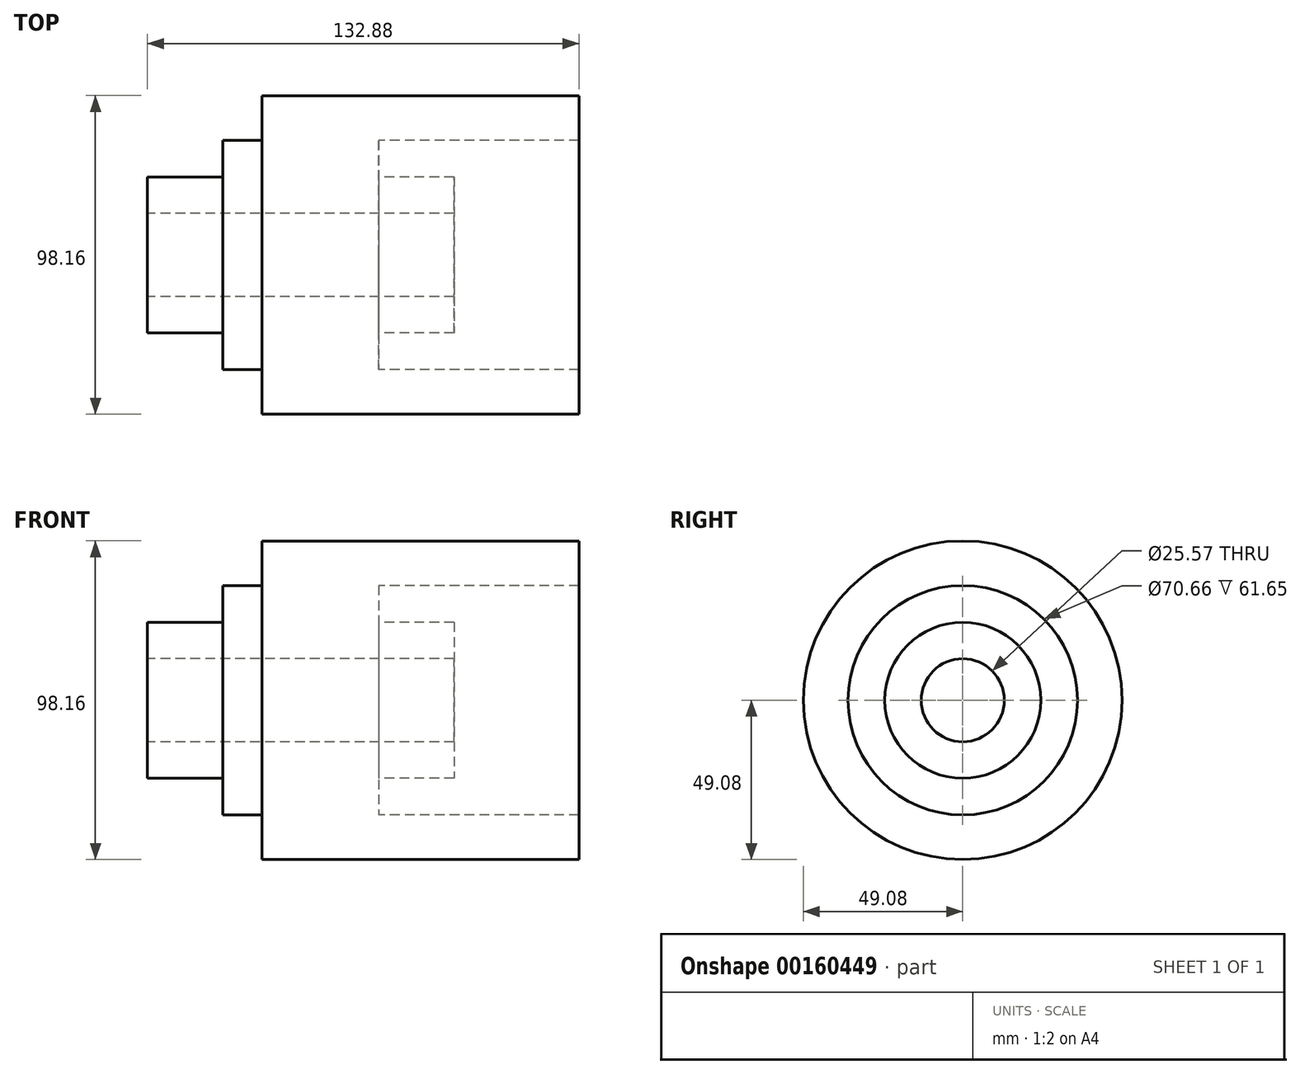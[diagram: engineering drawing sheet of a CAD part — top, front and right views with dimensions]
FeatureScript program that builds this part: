
annotation { "Feature Type Name" : "Feature", "Feature Type Description" : "" }
export const myFeature = defineFeature(function(context is Context, id is Id, definition is map)
    precondition{}
    {
        {
            var Q0;
            Q0=qCreatedBy(makeId("Front.planeOp"),FACE);
            var sketch = newSketch(context, id + "F0", { "sketchPlane" : qUnion([Q0])});
            skLineSegment(sketch, "E0", {"start": v(0, 0) * mm, "end": v(-47.2, 0) * mm});
            skLineSegment(sketch, "E1", {"start": v(-47.2, 0) * mm, "end": v(-47.2, 24.02) * mm});
            skLineSegment(sketch, "E2", {"start": v(-47.2, 24.02) * mm, "end": v(-24.02, 24.02) * mm});
            skLineSegment(sketch, "E3", {"start": v(-24.02, 24.02) * mm, "end": v(-24.02, 35.33) * mm});
            skLineSegment(sketch, "E4", {"start": v(-24.02, 35.33) * mm, "end": v(-12.01, 35.33) * mm});
            skLineSegment(sketch, "E5", {"start": v(12.01, 35.33) * mm, "end": v(24.02, 35.33) * mm});
            skLineSegment(sketch, "E6", {"start": v(24.02, 35.33) * mm, "end": v(24.02, 24.02) * mm});
            skLineSegment(sketch, "E7", {"start": v(24.02, 24.02) * mm, "end": v(47.2, 24.02) * mm});
            skLineSegment(sketch, "E8", {"start": v(47.2, 24.02) * mm, "end": v(47.2, 0) * mm});
            skLineSegment(sketch, "E9", {"start": v(0, 0) * mm, "end": v(47.2, 0) * mm});
            skLineSegment(sketch, "E10", {"start": v(-12.01, 35.33) * mm, "end": v(-12.01, 49.08) * mm});
            skLineSegment(sketch, "E11", {"start": v(-12.01, 49.08) * mm, "end": v(0, 49.08) * mm});
            skLineSegment(sketch, "E12", {"start": v(0, 49.08) * mm, "end": v(12.01, 49.08) * mm});
            skPoint(sketch, "E12.endSnap0", {"position": v(12.01, 35.33) * mm});
            skLineSegment(sketch, "E13", {"start": v(12.01, 49.08) * mm, "end": v(12.01, 35.33) * mm});
            skPoint(sketch, "E14.orphan", {"position": v(0, 35.33) * mm});
            skSolve(sketch);
        }
        {
            var Q0;
            Q0=makeQuery(id+"F0.imprint","IMPRINT",FACE,{"disambiguationData":[TD([[makeQuery(id+"F0.imprint","IMPRINT",EDGE,{"derivedFrom":sQuery(id+"F0.wireOp",EDGE,"E0")}),-1.0]])]});
            var Q1;
            Q1=sQuery(id+"F0.wireOp",EDGE,"E9");
            revolve(context, id + "F1", {"entities" : qUnion([Q0]), "axis" : qUnion([Q1]), "revolveType" : RevolveType.FULL});
        }
        {
            var Q0;
            Q0=makeQuery(id+"F1.opRevolve","SWEPT_FACE",FACE,{"disambiguationData":[OSD([sQuery(id+"F0.wireOp",EDGE,"E1")])]});
            var sketch = newSketch(context, id + "F2", { "sketchPlane" : qUnion([Q0])});
            skCircle(sketch, "E15", {"center": v(0, 0) * mm, "radius": 12.79 * mm});
            skSolve(sketch);
        }
        {
            var Q0;
            Q0=makeQuery(id+"F2.imprint","IMPRINT",FACE,{"disambiguationData":[TD([[makeQuery(id+"F2.imprint","IMPRINT",EDGE,{"derivedFrom":sQuery(id+"F2.wireOp",EDGE,"E15")}),1.0]])]});
            extrude(context, id + "F3", {"entities" : qUnion([Q0]), "operationType" : NewBodyOperationType.REMOVE, "endBound" : BoundingType.THROUGH_ALL, "oppositeDirection" : true, "depth" : 25.4 * mm});
        }
        {
            var Q0;
            Q0=makeQuery(id+"F1.opRevolve","SWEPT_FACE",FACE,{"disambiguationData":[OSD([sQuery(id+"F0.wireOp",EDGE,"E13")])]});
            var sketch = newSketch(context, id + "F4", { "sketchPlane" : qUnion([Q0])});
            skCircle(sketch, "E16.0", {"center": v(0, 0) * mm, "radius": 35.33 * mm});
            skCircle(sketch, "E17.0", {"center": v(0, 0) * mm, "radius": 49.08 * mm});
            skSolve(sketch);
        }
        {
            var Q0;
            Q0=makeQuery(id+"F4.imprint","IMPRINT",FACE,{"disambiguationData":[TD([[makeQuery(id+"F4.imprint","IMPRINT",EDGE,{"derivedFrom":sQuery(id+"F4.wireOp",EDGE,"E16.0")}),1.0]])]});
            extrude(context, id + "F5", {"entities" : qUnion([Q0]), "operationType" : NewBodyOperationType.ADD, "depth" : 73.66 * mm});
        }
    });
